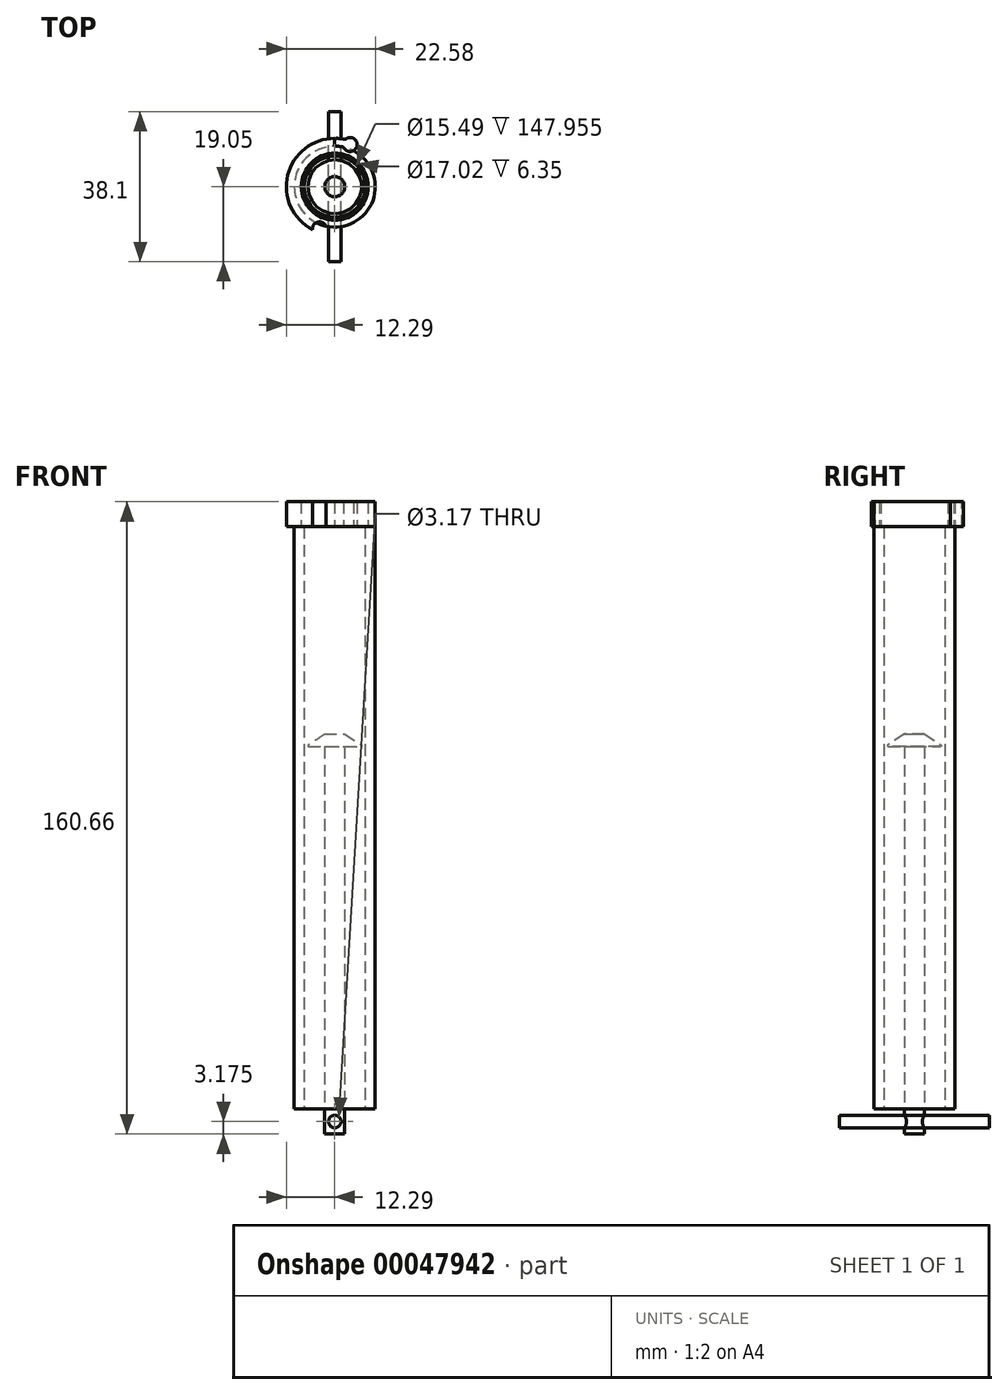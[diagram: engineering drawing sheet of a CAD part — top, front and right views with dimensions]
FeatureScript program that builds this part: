
annotation { "Feature Type Name" : "Feature", "Feature Type Description" : "" }
export const myFeature = defineFeature(function(context is Context, id is Id, definition is map)
    precondition{}
    {
        {
            var Q0;
            Q0=qCreatedBy(makeId("Front.planeOp"),FACE);
            var sketch = newSketch(context, id + "F0", { "sketchPlane" : qUnion([Q0])});
            skLineSegment(sketch, "E0", {"start": v(10.29, 0) * mm, "end": v(10.29, 147.96) * mm});
            skLineSegment(sketch, "E1", {"start": v(7.75, 147.96) * mm, "end": v(10.29, 147.96) * mm});
            skLineSegment(sketch, "E2", {"start": v(7.75, 147.96) * mm, "end": v(7.75, 0) * mm});
            skLineSegment(sketch, "E3", {"start": v(10.29, 0) * mm, "end": v(7.75, 0) * mm});
            skLineSegment(sketch, "E4", {"start": v(0, -6.35) * mm, "end": v(2.54, -6.35) * mm});
            skLineSegment(sketch, "E5", {"start": v(2.54, -6.35) * mm, "end": v(2.54, 92.08) * mm});
            skLineSegment(sketch, "E6", {"start": v(2.54, 92.08) * mm, "end": v(7.43, 92.08) * mm});
            skLineSegment(sketch, "E7", {"start": v(7.43, 92.08) * mm, "end": v(2.54, 95.25) * mm});
            skLineSegment(sketch, "E8", {"start": v(2.54, 95.25) * mm, "end": v(0, 95.25) * mm});
            skCircle(sketch, "E9", {"center": v(0, -3.18) * mm, "radius": 1.59 * mm});
            skLineSegment(sketch, "E10", {"start": v(0, -6.35) * mm, "end": v(0, 95.25) * mm});
            skSolve(sketch);
        }
        {
            var Q0;
            {var subQ4=sQuery(id+"F0.wireOp",EDGE,"E4");Q0=makeQuery(id+"F0.imprint","IMPRINT",FACE,{"disambiguationData":[TD([[makeQuery(id+"F0.imprint","IMPRINT",EDGE,{"derivedFrom":subQ4}),1.0]])]});}
            var Q1;
            {var subQ0=sQuery(id+"F0.wireOp",EDGE,"E10");var subQ1=sQuery(id+"F0.wireOp",EDGE,"E9");var subQ2=makeQuery(id+"F0.imprint","INTERSECT",VERTEX,{"disambiguationData":[OD(0.0)],"derivedFrom":[subQ1,subQ0]});Q1=makeQuery(id+"F0.imprint","IMPRINT",FACE,{"disambiguationData":[TD([[makeQuery(id+"F0.imprint","IMPRINT",EDGE,{"disambiguationData":[TD([[subQ2,-1.0]])],"derivedFrom":subQ1}),1.0]])]});}
            var Q2;
            Q2=sQuery(id+"F0.wireOp",EDGE,"E10");
            revolve(context, id + "F1", {"entities" : qUnion([Q0, Q1]), "axis" : qUnion([Q2]), "revolveType" : RevolveType.FULL});
        }
        {
            var Q0;
            Q0=makeQuery(id+"F0.imprint","IMPRINT",FACE,{"disambiguationData":[TD([[makeQuery(id+"F0.imprint","IMPRINT",EDGE,{"derivedFrom":sQuery(id+"F0.wireOp",EDGE,"E0")}),1.0]])]});
            var Q1;
            Q1=sQuery(id+"F0.wireOp",EDGE,"E10");
            revolve(context, id + "F2", {"entities" : qUnion([Q0]), "axis" : qUnion([Q1]), "revolveType" : RevolveType.FULL});
        }
        {
            var Q0;
            Q0=makeQuery(id+"F1.opRevolve","SWEPT_EDGE",EDGE,{"disambiguationData":[OSD([sQuery(id+"F0.wireOp",EDGE,"E6"),sQuery(id+"F0.wireOp",EDGE,"E7")])]});
            fillet(context, id + "F3", {"entities" : qUnion([Q0]), "radius" : 0.25 * mm, "tangentPropagation" : true, "allowEdgeOverflow" : false});
        }
        {
            var Q0;
            {var subQ0=sQuery(id+"F0.wireOp",EDGE,"E10");var subQ1=sQuery(id+"F0.wireOp",EDGE,"E9");var subQ2=makeQuery(id+"F0.imprint","INTERSECT",VERTEX,{"disambiguationData":[OD(0.0)],"derivedFrom":[subQ1,subQ0]});Q0=makeQuery(id+"F0.imprint","IMPRINT",FACE,{"disambiguationData":[TD([[makeQuery(id+"F0.imprint","IMPRINT",EDGE,{"disambiguationData":[TD([[subQ2,1.0]])],"derivedFrom":subQ1}),1.0]])]});}
            var Q1;
            {var subQ0=sQuery(id+"F0.wireOp",EDGE,"E10");var subQ1=sQuery(id+"F0.wireOp",EDGE,"E9");var subQ2=makeQuery(id+"F0.imprint","INTERSECT",VERTEX,{"disambiguationData":[OD(0.0)],"derivedFrom":[subQ1,subQ0]});Q1=makeQuery(id+"F0.imprint","IMPRINT",FACE,{"disambiguationData":[TD([[makeQuery(id+"F0.imprint","IMPRINT",EDGE,{"disambiguationData":[TD([[subQ2,-1.0]])],"derivedFrom":subQ1}),1.0]])]});}
            extrude(context, id + "F4", {"entities" : qUnion([Q0, Q1]), "operationType" : NewBodyOperationType.REMOVE, "endBound" : BoundingType.SYMMETRIC, "oppositeDirection" : true, "depth" : 5.08 * mm});
        }
        {
            var Q0;
            {var subQ0=sQuery(id+"F0.wireOp",EDGE,"E10");var subQ1=sQuery(id+"F0.wireOp",EDGE,"E9");var subQ2=makeQuery(id+"F0.imprint","INTERSECT",VERTEX,{"disambiguationData":[OD(0.0)],"derivedFrom":[subQ1,subQ0]});Q0=makeQuery(id+"F0.imprint","IMPRINT",FACE,{"disambiguationData":[TD([[makeQuery(id+"F0.imprint","IMPRINT",EDGE,{"disambiguationData":[TD([[subQ2,-1.0]])],"derivedFrom":subQ1}),1.0]])]});}
            var Q1;
            {var subQ0=sQuery(id+"F0.wireOp",EDGE,"E10");var subQ1=sQuery(id+"F0.wireOp",EDGE,"E9");var subQ2=makeQuery(id+"F0.imprint","INTERSECT",VERTEX,{"disambiguationData":[OD(0.0)],"derivedFrom":[subQ1,subQ0]});Q1=makeQuery(id+"F0.imprint","IMPRINT",FACE,{"disambiguationData":[TD([[makeQuery(id+"F0.imprint","IMPRINT",EDGE,{"disambiguationData":[TD([[subQ2,1.0]])],"derivedFrom":subQ1}),1.0]])]});}
            extrude(context, id + "F5", {"entities" : qUnion([Q0, Q1]), "endBound" : BoundingType.SYMMETRIC, "depth" : 38.1 * mm});
        }
        {
            var Q0;
            Q0=makeQuery(id+"F2.opRevolve","SWEPT_FACE",FACE,{"disambiguationData":[OSD([sQuery(id+"F0.wireOp",EDGE,"E1")])]});
            var sketch = newSketch(context, id + "F6", { "sketchPlane" : qUnion([Q0])});
            skCircle(sketch, "E11", {"center": v(0, 0) * mm, "radius": 14.29 * mm});
            skCircle(sketch, "E12", {"center": v(0, 0) * mm, "radius": 11.4 * mm, "construction": true});
            skCircle(sketch, "E13", {"center": v(3.9, 10.71) * mm, "radius": 1.78 * mm});
            skLineSegment(sketch, "E14", {"start": v(0, 0) * mm, "end": v(0, 14.29) * mm});
            skCircle(sketch, "E15.0", {"center": v(0, 0) * mm, "radius": 12.29 * mm});
            skCircle(sketch, "E16.0", {"center": v(0, 0) * mm, "radius": 10.5 * mm});
            skLineSegment(sketch, "E17", {"start": v(0, 0) * mm, "end": v(3.9, 10.71) * mm, "construction": true});
            skLineSegment(sketch, "E18", {"start": v(0, 0) * mm, "end": v(-5.21, 1.9) * mm, "construction": true});
            skCircle(sketch, "E19.MirrorC", {"center": v(-3.9, -10.71) * mm, "radius": 1.78 * mm});
            skLineSegment(sketch, "E20", {"start": v(0, 12.29) * mm, "end": v(0, 14.29) * mm});
            skLineSegment(sketch, "E21", {"start": v(0, 10.29) * mm, "end": v(0, 7.14) * mm});
            skLineSegment(sketch, "E22", {"start": v(0, 0) * mm, "end": v(0, -14.29) * mm});
            skCircle(sketch, "E23", {"center": v(0, 0) * mm, "radius": 8.5 * mm});
            skSolve(sketch);
        }
        {
            var Q0;
            {var subQ0=sQuery(id+"F6.wireOp",EDGE,"E16.0");var subQ1=sQuery(id+"F6.wireOp",EDGE,"E13");var subQ2=makeQuery(id+"F6.imprint","INTERSECT",VERTEX,{"disambiguationData":[OD(0.0)],"derivedFrom":[subQ1,subQ0]});Q0=makeQuery(id+"F6.imprint","IMPRINT",FACE,{"disambiguationData":[TD([[makeQuery(id+"F6.imprint","IMPRINT",EDGE,{"disambiguationData":[TD([[subQ2,-1.0]])],"derivedFrom":subQ0}),1.0]])]});}
            var Q1;
            {var subQ0=sQuery(id+"F6.wireOp",EDGE,"E16.0");var subQ1=sQuery(id+"F6.wireOp",EDGE,"E13");var subQ2=makeQuery(id+"F6.imprint","INTERSECT",VERTEX,{"disambiguationData":[OD(0.0)],"derivedFrom":[subQ1,subQ0]});Q1=makeQuery(id+"F6.imprint","IMPRINT",FACE,{"disambiguationData":[TD([[makeQuery(id+"F6.imprint","IMPRINT",EDGE,{"disambiguationData":[TD([[subQ2,1.0]])],"derivedFrom":subQ0}),1.0]])]});}
            var Q2;
            {var subQ0=sQuery(id+"F6.wireOp",EDGE,"E13");var subQ1=makeQuery(id+"F2.opRevolve","SWEPT_EDGE",EDGE,{"disambiguationData":[OSD([sQuery(id+"F0.wireOp",EDGE,"E0"),sQuery(id+"F0.wireOp",EDGE,"E1")])]});var subQ2=makeQuery(id+"F6.imprint","INTERSECT",VERTEX,{"disambiguationData":[OD(0.0)],"derivedFrom":[subQ1,subQ0]});Q2=makeQuery(id+"F6.imprint","IMPRINT",FACE,{"disambiguationData":[TD([[makeQuery(id+"F6.imprint","IMPRINT",EDGE,{"disambiguationData":[TD([[subQ2,-1.0]])],"derivedFrom":subQ0}),1.0]])]});}
            var Q3;
            {var subQ0=sQuery(id+"F6.wireOp",EDGE,"E15.0");var subQ1=sQuery(id+"F6.wireOp",EDGE,"E13");var subQ2=makeQuery(id+"F6.imprint","INTERSECT",VERTEX,{"disambiguationData":[OD(0.0)],"derivedFrom":[subQ1,subQ0]});Q3=makeQuery(id+"F6.imprint","IMPRINT",FACE,{"disambiguationData":[TD([[makeQuery(id+"F6.imprint","IMPRINT",EDGE,{"disambiguationData":[TD([[subQ2,-1.0]])],"derivedFrom":subQ1}),1.0]])]});}
            var Q4;
            {var subQ0=sQuery(id+"F6.wireOp",EDGE,"E15.0");var subQ1=sQuery(id+"F6.wireOp",EDGE,"E13");var subQ2=makeQuery(id+"F6.imprint","INTERSECT",VERTEX,{"disambiguationData":[OD(0.0)],"derivedFrom":[subQ1,subQ0]});Q4=makeQuery(id+"F6.imprint","IMPRINT",FACE,{"disambiguationData":[TD([[makeQuery(id+"F6.imprint","IMPRINT",EDGE,{"disambiguationData":[TD([[subQ2,1.0]])],"derivedFrom":subQ1}),1.0]])]});}
            var Q5;
            {var subQ0=sQuery(id+"F6.wireOp",EDGE,"E15.0");var subQ1=sQuery(id+"F6.wireOp",EDGE,"E13");var subQ2=makeQuery(id+"F6.imprint","INTERSECT",VERTEX,{"disambiguationData":[OD(0.0)],"derivedFrom":[subQ1,subQ0]});Q5=makeQuery(id+"F6.imprint","IMPRINT",FACE,{"disambiguationData":[TD([[makeQuery(id+"F6.imprint","IMPRINT",EDGE,{"disambiguationData":[TD([[subQ2,-1.0]])],"derivedFrom":subQ1}),-1.0]])]});}
            extrude(context, id + "F7", {"entities" : qUnion([Q0, Q1, Q2, Q3, Q4, Q5]), "offsetDistance" : 25.4 * mm, "depth" : 6.35 * mm});
        }
        {
            var Q0;
            {var subQ4=sQuery(id+"F6.wireOp",EDGE,"E20");Q0=makeQuery(id+"F6.imprint","IMPRINT",FACE,{"disambiguationData":[TD([[makeQuery(id+"F6.imprint","IMPRINT",EDGE,{"derivedFrom":subQ4}),1.0]])]});}
            var Q1;
            {var subQ1=sQuery(id+"F6.wireOp",EDGE,"E14");var subQ3=sQuery(id+"F6.wireOp",EDGE,"E16.0");var subQ4=makeQuery(id+"F6.imprint","INTERSECT",VERTEX,{"derivedFrom":[subQ1,subQ3]});Q1=makeQuery(id+"F6.imprint","IMPRINT",FACE,{"disambiguationData":[TD([[makeQuery(id+"F6.imprint","IMPRINT",EDGE,{"disambiguationData":[TD([[subQ4,-1.0]])],"derivedFrom":subQ3}),-1.0]])]});}
            var Q2;
            {var subQ0=sQuery(id+"F6.wireOp",EDGE,"E23");var subQ1=sQuery(id+"F6.wireOp",EDGE,"E21");var subQ2=makeQuery(id+"F6.imprint","INTERSECT",VERTEX,{"derivedFrom":[subQ1,subQ0]});Q2=makeQuery(id+"F6.imprint","IMPRINT",FACE,{"disambiguationData":[TD([[makeQuery(id+"F6.imprint","IMPRINT",EDGE,{"disambiguationData":[TD([[subQ2,-1.0]])],"derivedFrom":subQ0}),-1.0]])]});}
            var Q3;
            {var subQ0=sQuery(id+"F6.wireOp",EDGE,"E19.MirrorC");var subQ1=sQuery(id+"F6.wireOp",EDGE,"E15.0");var subQ2=makeQuery(id+"F6.imprint","INTERSECT",VERTEX,{"disambiguationData":[OD(0.0)],"derivedFrom":[subQ1,subQ0]});Q3=makeQuery(id+"F6.imprint","IMPRINT",FACE,{"disambiguationData":[TD([[makeQuery(id+"F6.imprint","IMPRINT",EDGE,{"disambiguationData":[TD([[subQ2,-1.0]])],"derivedFrom":subQ1}),-1.0]])]});}
            var Q4;
            {var subQ0=sQuery(id+"F6.wireOp",EDGE,"E19.MirrorC");var subQ1=sQuery(id+"F6.wireOp",EDGE,"E16.0");var subQ2=makeQuery(id+"F6.imprint","INTERSECT",VERTEX,{"disambiguationData":[OD(0.0)],"derivedFrom":[subQ1,subQ0]});Q4=makeQuery(id+"F6.imprint","IMPRINT",FACE,{"disambiguationData":[TD([[makeQuery(id+"F6.imprint","IMPRINT",EDGE,{"disambiguationData":[TD([[subQ2,-1.0]])],"derivedFrom":subQ1}),1.0]])]});}
            var Q5;
            {var subQ0=sQuery(id+"F6.wireOp",EDGE,"E19.MirrorC");var subQ1=makeQuery(id+"F2.opRevolve","SWEPT_EDGE",EDGE,{"disambiguationData":[OSD([sQuery(id+"F0.wireOp",EDGE,"E0"),sQuery(id+"F0.wireOp",EDGE,"E1")])]});var subQ2=makeQuery(id+"F6.imprint","INTERSECT",VERTEX,{"disambiguationData":[OD(0.0)],"derivedFrom":[subQ1,subQ0]});Q5=makeQuery(id+"F6.imprint","IMPRINT",FACE,{"disambiguationData":[TD([[makeQuery(id+"F6.imprint","IMPRINT",EDGE,{"disambiguationData":[TD([[subQ2,-1.0]])],"derivedFrom":subQ0}),-1.0]])]});}
            var Q6;
            {var subQ0=sQuery(id+"F6.wireOp",EDGE,"E14");var subQ3=sQuery(id+"F6.wireOp",EDGE,"E16.0");var subQ4=makeQuery(id+"F6.imprint","INTERSECT",VERTEX,{"derivedFrom":[subQ0,subQ3]});Q6=makeQuery(id+"F6.imprint","IMPRINT",FACE,{"disambiguationData":[TD([[makeQuery(id+"F6.imprint","IMPRINT",EDGE,{"disambiguationData":[TD([[subQ4,-1.0]])],"derivedFrom":subQ3}),1.0]])]});}
            var Q7;
            {var subQ0=sQuery(id+"F6.wireOp",EDGE,"E19.MirrorC");var subQ1=sQuery(id+"F6.wireOp",EDGE,"E15.0");var subQ2=makeQuery(id+"F6.imprint","INTERSECT",VERTEX,{"disambiguationData":[OD(0.0)],"derivedFrom":[subQ1,subQ0]});Q7=makeQuery(id+"F6.imprint","IMPRINT",FACE,{"disambiguationData":[TD([[makeQuery(id+"F6.imprint","IMPRINT",EDGE,{"disambiguationData":[TD([[subQ2,-1.0]])],"derivedFrom":subQ1}),1.0]])]});}
            var Q8;
            {var subQ0=sQuery(id+"F6.wireOp",EDGE,"E19.MirrorC");var subQ1=sQuery(id+"F6.wireOp",EDGE,"E15.0");var subQ2=makeQuery(id+"F6.imprint","INTERSECT",VERTEX,{"disambiguationData":[OD(1.0)],"derivedFrom":[subQ1,subQ0]});Q8=makeQuery(id+"F6.imprint","IMPRINT",FACE,{"disambiguationData":[TD([[makeQuery(id+"F6.imprint","IMPRINT",EDGE,{"disambiguationData":[TD([[subQ2,-1.0]])],"derivedFrom":subQ1}),1.0]])]});}
            var Q9;
            {var subQ0=sQuery(id+"F6.wireOp",EDGE,"E19.MirrorC");var subQ1=sQuery(id+"F6.wireOp",EDGE,"E16.0");var subQ2=makeQuery(id+"F6.imprint","INTERSECT",VERTEX,{"disambiguationData":[OD(1.0)],"derivedFrom":[subQ1,subQ0]});Q9=makeQuery(id+"F6.imprint","IMPRINT",FACE,{"disambiguationData":[TD([[makeQuery(id+"F6.imprint","IMPRINT",EDGE,{"disambiguationData":[TD([[subQ2,-1.0]])],"derivedFrom":subQ1}),1.0]])]});}
            var Q10;
            Q10=makeQuery(id+"F7.opExtrude","CAP_FACE",FACE,{"disambiguationData":[OSD([sQuery(id+"F0.wireOp",EDGE,"E0"),sQuery(id+"F0.wireOp",EDGE,"E1"),sQuery(id+"F6.wireOp",EDGE,"E13"),sQuery(id+"F6.wireOp",EDGE,"E14"),sQuery(id+"F6.wireOp",EDGE,"E15.0")])],"isStart":false});
            extrude(context, id + "F8", {"entities" : qUnion([Q0, Q1, Q2, Q3, Q4, Q5, Q6, Q7, Q8, Q9]), "endBound" : BoundingType.UP_TO_SURFACE, "depth" : 25.4 * mm, "endBoundEntityFace" : qUnion([Q10]), "offsetDistance" : 25.4 * mm});
        }
        {
            var Q0;
            Q0=makeQuery(id+"F7.opExtrude","SWEPT_BODY",BODY,{"disambiguationData":[OSD([sQuery(id+"F0.wireOp",EDGE,"E0"),sQuery(id+"F0.wireOp",EDGE,"E1"),sQuery(id+"F6.wireOp",EDGE,"E13"),sQuery(id+"F6.wireOp",EDGE,"E14"),sQuery(id+"F6.wireOp",EDGE,"E15.0")])]});
            var Q1;
            Q1=makeQuery(id+"F2.opRevolve","SWEPT_FACE",FACE,{"disambiguationData":[OSD([sQuery(id+"F0.wireOp",EDGE,"E2")])]});
            circularPattern(context, id + "F9", {"entities" : qUnion([Q0]), "axis" : qUnion([Q1]), "angle" : 360 * degree, "instanceCount" : 2, "equalSpace" : true});
        }
        {
            var Q0;
            Q0=makeQuery(id+"F9.opPattern","COPY",BODY,{"derivedFrom":makeQuery(id+"F7.opExtrude","SWEPT_BODY",BODY,{"disambiguationData":[OSD([sQuery(id+"F0.wireOp",EDGE,"E0"),sQuery(id+"F0.wireOp",EDGE,"E1"),sQuery(id+"F6.wireOp",EDGE,"E13"),sQuery(id+"F6.wireOp",EDGE,"E14"),sQuery(id+"F6.wireOp",EDGE,"E15.0")])]}),"instanceName":"1"});
            var Q1;
            Q1=makeQuery(id+"F8.opExtrude","SWEPT_BODY",BODY,{"disambiguationData":[OSD([sQuery(id+"F6.wireOp",EDGE,"E11"),sQuery(id+"F6.wireOp",EDGE,"E14"),sQuery(id+"F6.wireOp",EDGE,"E20"),sQuery(id+"F6.wireOp",EDGE,"E21"),sQuery(id+"F6.wireOp",EDGE,"E22"),sQuery(id+"F6.wireOp",EDGE,"E23")])]});
            booleanBodies(context, id + "F10", {"operationType" : BooleanOperationType.SUBTRACTION, "tools" : qUnion([Q0]), "targets" : qUnion([Q1])});
        }
        {
            var Q0;
            Q0=makeQuery(id+"F7.opExtrude","SWEPT_EDGE",EDGE,{"disambiguationData":[OSD([sQuery(id+"F0.wireOp",EDGE,"E0"),sQuery(id+"F0.wireOp",EDGE,"E1"),sQuery(id+"F6.wireOp",EDGE,"E13")])]});
            var Q1;
            Q1=makeQuery(id+"F7.opExtrude","SWEPT_EDGE",EDGE,{"disambiguationData":[OSD([sQuery(id+"F6.wireOp",EDGE,"E13"),sQuery(id+"F6.wireOp",EDGE,"E15.0")])]});
            var Q2;
            Q2=makeQuery(id+"F7.opExtrude","SWEPT_EDGE",EDGE,{"disambiguationData":[OSD([sQuery(id+"F0.wireOp",EDGE,"E0"),sQuery(id+"F0.wireOp",EDGE,"E1"),sQuery(id+"F6.wireOp",EDGE,"E14"),sQuery(id+"F6.wireOp",EDGE,"E21")])]});
            var Q3;
            Q3=makeQuery(id+"F7.opExtrude","SWEPT_EDGE",EDGE,{"disambiguationData":[OSD([sQuery(id+"F6.wireOp",EDGE,"E14"),sQuery(id+"F6.wireOp",EDGE,"E15.0"),sQuery(id+"F6.wireOp",EDGE,"E20")])]});
            var Q4;
            Q4=makeQuery(id+"F10.opBoolean","COPY",EDGE,{"derivedFrom":makeQuery(id+"F9.opPattern","COPY",EDGE,{"derivedFrom":makeQuery(id+"F7.opExtrude","SWEPT_EDGE",EDGE,{"disambiguationData":[OSD([sQuery(id+"F0.wireOp",EDGE,"E0"),sQuery(id+"F0.wireOp",EDGE,"E1"),sQuery(id+"F6.wireOp",EDGE,"E14"),sQuery(id+"F6.wireOp",EDGE,"E21")])]}),"instanceName":"1"})});
            var Q5;
            Q5=makeQuery(id+"F10.opBoolean","COPY",EDGE,{"derivedFrom":makeQuery(id+"F9.opPattern","COPY",EDGE,{"derivedFrom":makeQuery(id+"F7.opExtrude","SWEPT_EDGE",EDGE,{"disambiguationData":[OSD([sQuery(id+"F6.wireOp",EDGE,"E14"),sQuery(id+"F6.wireOp",EDGE,"E15.0"),sQuery(id+"F6.wireOp",EDGE,"E20")])]}),"instanceName":"1"})});
            var Q6;
            Q6=makeQuery(id+"F10.opBoolean","COPY",EDGE,{"derivedFrom":makeQuery(id+"F9.opPattern","COPY",EDGE,{"derivedFrom":makeQuery(id+"F7.opExtrude","SWEPT_EDGE",EDGE,{"disambiguationData":[OSD([sQuery(id+"F0.wireOp",EDGE,"E0"),sQuery(id+"F0.wireOp",EDGE,"E1"),sQuery(id+"F6.wireOp",EDGE,"E13")])]}),"instanceName":"1"})});
            var Q7;
            Q7=makeQuery(id+"F10.opBoolean","COPY",EDGE,{"derivedFrom":makeQuery(id+"F9.opPattern","COPY",EDGE,{"derivedFrom":makeQuery(id+"F7.opExtrude","SWEPT_EDGE",EDGE,{"disambiguationData":[OSD([sQuery(id+"F6.wireOp",EDGE,"E13"),sQuery(id+"F6.wireOp",EDGE,"E15.0")])]}),"instanceName":"1"})});
            var Q8;
            Q8=makeQuery(id+"F8.opExtrude","SWEPT_EDGE",EDGE,{"disambiguationData":[OSD([sQuery(id+"F6.wireOp",EDGE,"E11"),sQuery(id+"F6.wireOp",EDGE,"E22")])]});
            var Q9;
            Q9=makeQuery(id+"F8.opExtrude","SWEPT_EDGE",EDGE,{"disambiguationData":[OSD([sQuery(id+"F6.wireOp",EDGE,"E22"),sQuery(id+"F6.wireOp",EDGE,"E23")])]});
            var Q10;
            Q10=makeQuery(id+"F8.opExtrude","SWEPT_EDGE",EDGE,{"disambiguationData":[OSD([sQuery(id+"F6.wireOp",EDGE,"E21"),sQuery(id+"F6.wireOp",EDGE,"E23")])]});
            var Q11;
            Q11=makeQuery(id+"F8.opExtrude","SWEPT_EDGE",EDGE,{"disambiguationData":[OSD([sQuery(id+"F6.wireOp",EDGE,"E11"),sQuery(id+"F6.wireOp",EDGE,"E20")])]});
            fillet(context, id + "F11", {"entities" : qUnion([Q0, Q1, Q2, Q3, Q4, Q5, Q6, Q7, Q8, Q9, Q10, Q11]), "tangentPropagation" : true, "radius" : 0.5 * mm, "defaultsChanged" : false, "vertexSettings" : [], "allowEdgeOverflow" : false});
        }
    });
